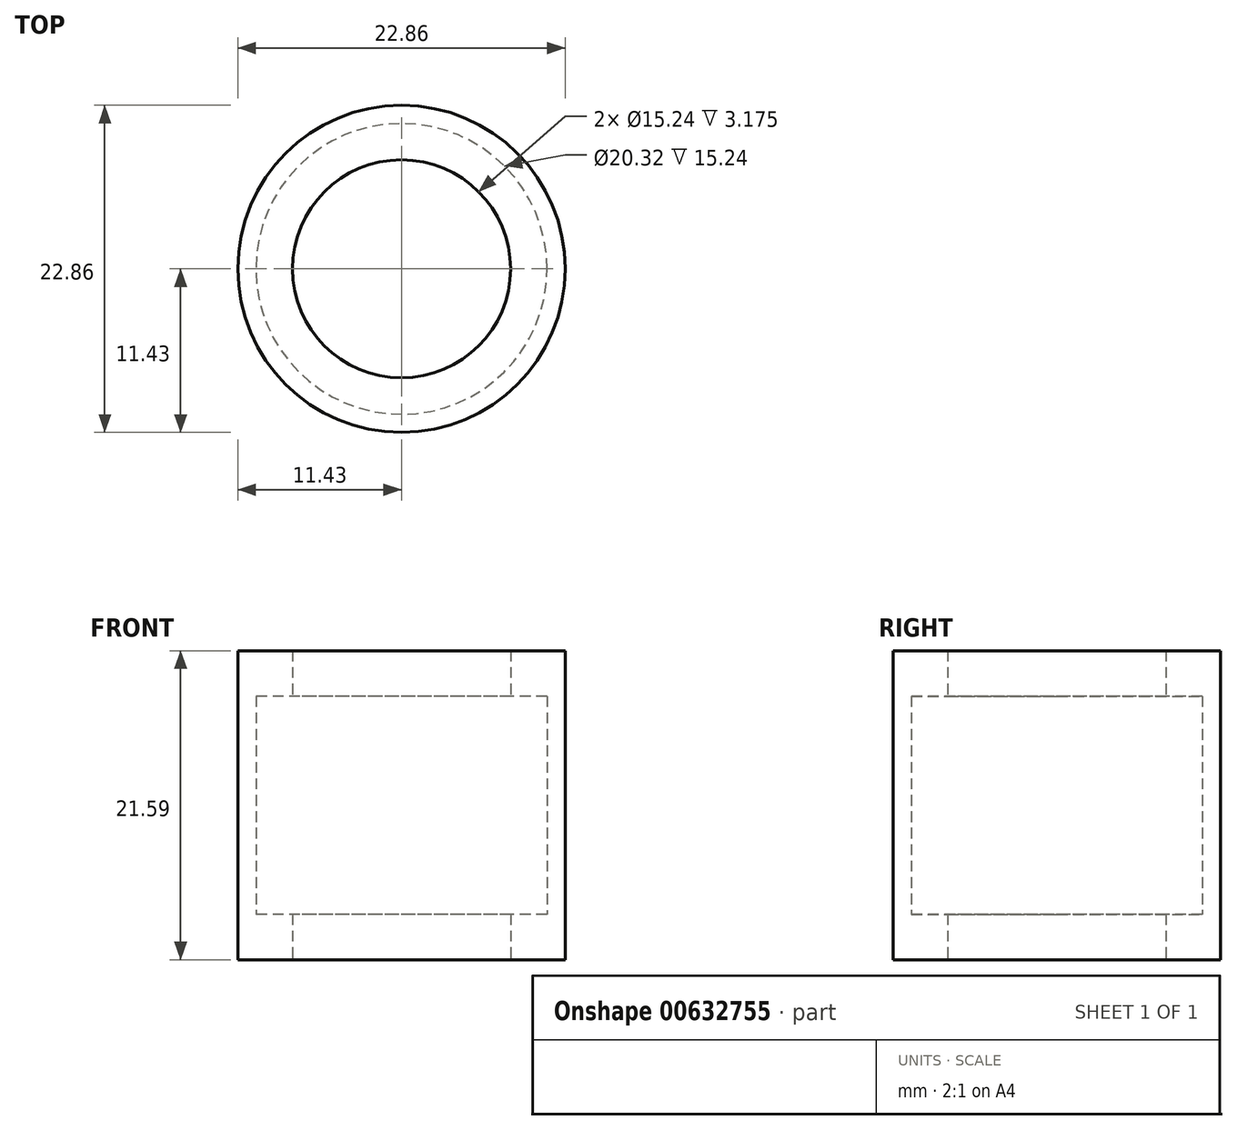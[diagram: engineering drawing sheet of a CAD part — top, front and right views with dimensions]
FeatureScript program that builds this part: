
annotation { "Feature Type Name" : "Feature", "Feature Type Description" : "" }
export const myFeature = defineFeature(function(context is Context, id is Id, definition is map)
    precondition{}
    {
        {
            var Q0;
            Q0=qCreatedBy(makeId("Top.planeOp"),FACE);
            var sketch = newSketch(context, id + "F0", { "sketchPlane" : qUnion([Q0])});
            skCircle(sketch, "E0", {"center": v(0, 0) * mm, "radius": 11.43 * mm});
            skCircle(sketch, "E1", {"center": v(0, 0) * mm, "radius": 7.62 * mm});
            skSolve(sketch);
        }
        {
            var Q0;
            Q0=makeQuery(id+"F0.imprint","IMPRINT",FACE,{"disambiguationData":[TD([[makeQuery(id+"F0.imprint","IMPRINT",EDGE,{"derivedFrom":sQuery(id+"F0.wireOp",EDGE,"E0")}),1.0]])]});
            extrude(context, id + "F1", {"entities" : qUnion([Q0]), "depth" : 3.17 * mm, "offsetDistance" : 25.4 * mm});
        }
        {
            var Q0;
            Q0=makeQuery(id+"F1.opExtrude","CAP_FACE",FACE,{"disambiguationData":[OSD([sQuery(id+"F0.wireOp",EDGE,"E0"),sQuery(id+"F0.wireOp",EDGE,"E1")])],"isStart":false});
            var sketch = newSketch(context, id + "F2", { "sketchPlane" : qUnion([Q0])});
            skCircle(sketch, "E2", {"center": v(0, 0) * mm, "radius": 11.43 * mm});
            skCircle(sketch, "E3", {"center": v(0, 0) * mm, "radius": 10.16 * mm});
            skSolve(sketch);
        }
        {
            var Q0;
            Q0=makeQuery(id+"F2.imprint","IMPRINT",FACE,{"disambiguationData":[TD([[makeQuery(id+"F2.imprint","IMPRINT",EDGE,{"derivedFrom":sQuery(id+"F2.wireOp",EDGE,"E2")}),1.0]])]});
            extrude(context, id + "F3", {"entities" : qUnion([Q0]), "operationType" : NewBodyOperationType.ADD, "depth" : 15.24 * mm, "offsetDistance" : 25.4 * mm});
        }
        {
            var Q0;
            Q0=makeQuery(id+"F3.opExtrude","CAP_FACE",FACE,{"disambiguationData":[OSD([sQuery(id+"F2.wireOp",EDGE,"E2"),sQuery(id+"F2.wireOp",EDGE,"E3")])],"isStart":false});
            var sketch = newSketch(context, id + "F4", { "sketchPlane" : qUnion([Q0])});
            skCircle(sketch, "E4", {"center": v(0, 0) * mm, "radius": 11.43 * mm});
            skCircle(sketch, "E5", {"center": v(0, 0) * mm, "radius": 7.62 * mm});
            skSolve(sketch);
        }
        {
            var Q0;
            Q0=makeQuery(id+"F4.imprint","IMPRINT",FACE,{"disambiguationData":[TD([[makeQuery(id+"F4.imprint","IMPRINT",EDGE,{"derivedFrom":sQuery(id+"F4.wireOp",EDGE,"E4")}),1.0]])]});
            var Q1;
            Q1=makeQuery(id+"F4.imprint","IMPRINT",FACE,{"disambiguationData":[TD([[makeQuery(id+"F4.imprint","IMPRINT",EDGE,{"derivedFrom":sQuery(id+"F4.wireOp",EDGE,"E5")}),-1.0]])]});
            extrude(context, id + "F5", {"entities" : qUnion([Q0, Q1]), "operationType" : NewBodyOperationType.ADD, "depth" : 3.17 * mm, "offsetDistance" : 25.4 * mm});
        }
    });
